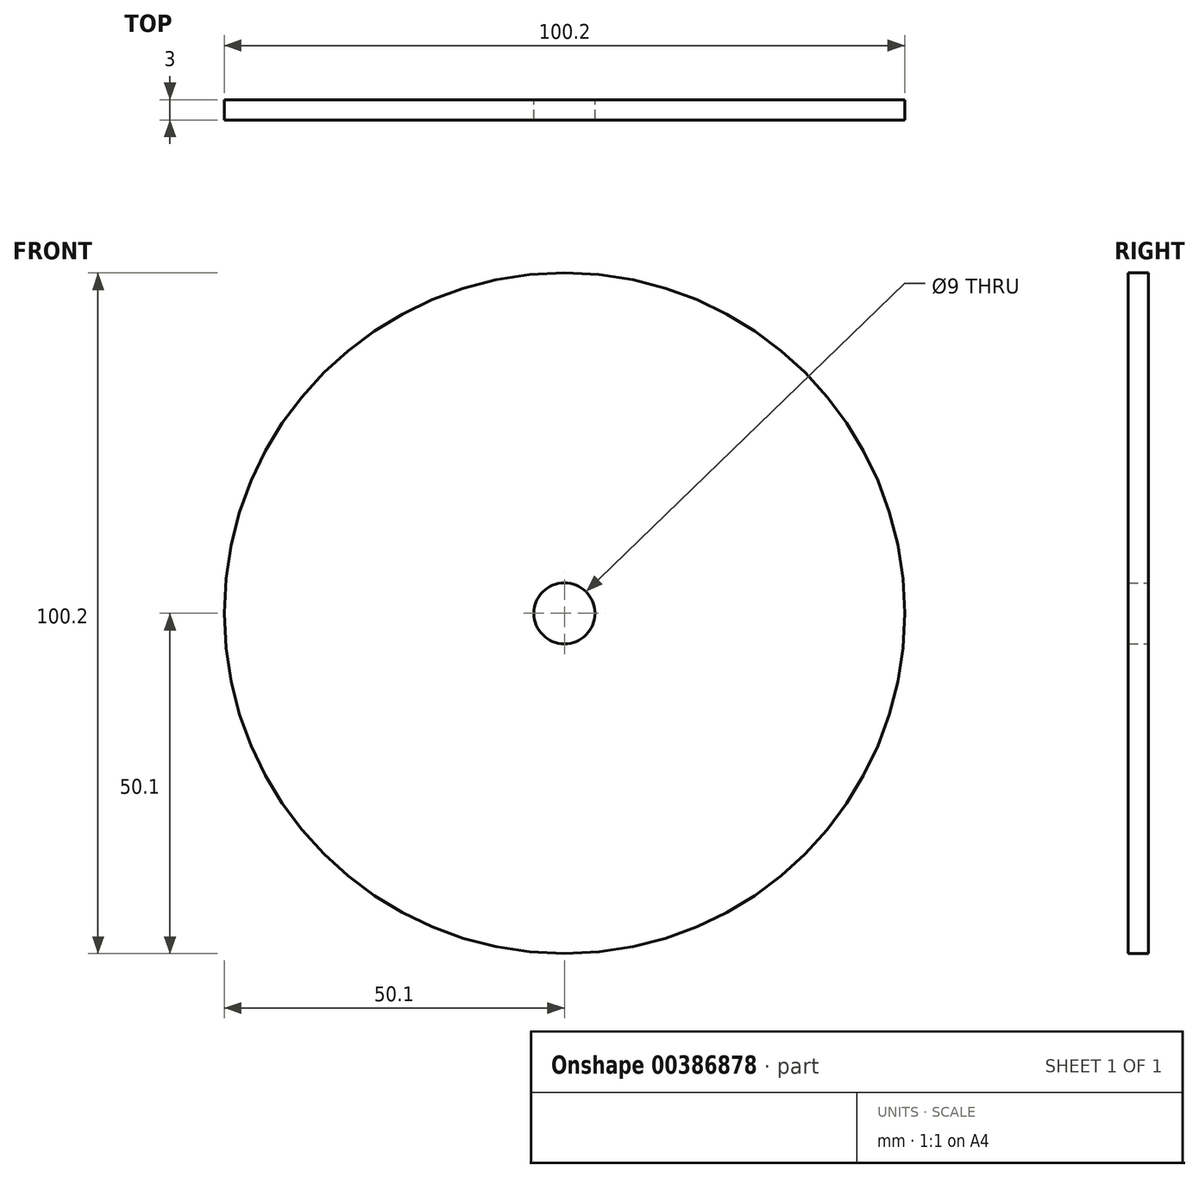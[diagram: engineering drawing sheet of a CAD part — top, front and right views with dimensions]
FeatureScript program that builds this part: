
annotation { "Feature Type Name" : "Feature", "Feature Type Description" : "" }
export const myFeature = defineFeature(function(context is Context, id is Id, definition is map)
    precondition{}
    {
        {
            var Q0;
            Q0=qCreatedBy(makeId("Front.planeOp"),FACE);
            var sketch = newSketch(context, id + "F0", { "sketchPlane" : qUnion([Q0])});
            skCircle(sketch, "E0", {"center": v(0, 0) * mm, "radius": 50.1 * mm});
            skCircle(sketch, "E1", {"center": v(0, 0) * mm, "radius": 4.5 * mm});
            skSolve(sketch);
        }
        {
            var Q0;
            Q0 = qSketchRegion(id + "F0", true);
            extrude(context, id + "F1", {"entities" : qUnion([Q0]), "depth" : 3 * mm});
        }
    });
